FCSTD DOCUMENT  (FreeCAD 0.18R16117 (Git))
Label: impianto_1
License: All rights reserved
LicenseURL: http://en.wikipedia.org/wiki/All_rights_reserved
objects: Sketcher::SketchObject×1, PartDesign::Body×1, Drawing::FeatureViewPart×1, Drawing::FeaturePage×1
note: 2 computed .brp shape members not serialized (recipe doc carries the construction recipe); baked Part::Feature solids carry a one-line shape summary decoded from their .brp

FEATURE [Sketcher::SketchObject] Sketch
  MapMode = 5
  Support = -> [XY_Plane]
  sketch-geometry (29):
    g0: LineSegment StartX=10 StartY=0 StartZ=0 EndX=10 EndY=17 EndZ=0
    g1: LineSegment StartX=0 StartY=17 StartZ=0 EndX=0 EndY=0 EndZ=0
    g2: LineSegment StartX=83.6635 StartY=45.5185 StartZ=0 EndX=83.6635 EndY=27.5185 EndZ=0
    g3: LineSegment StartX=63.9673 StartY=42.0455 StartZ=0 EndX=83.6635 EndY=45.5185 EndZ=0
    g4: LineSegment StartX=83.6635 StartY=27.5185 StartZ=0 EndX=63.9673 EndY=30.9915 EndZ=0
    g5: Circle CenterX=83.6635 CenterY=13.7593 CenterZ=0 NormalX=0 NormalY=0 NormalZ=1 AngleXU=0 Radius=3
    g6: LineSegment [constr] StartX=83.6635 StartY=16.7593 StartZ=0 EndX=83.6635 EndY=10.7593 EndZ=0
    g7: LineSegment StartX=0 StartY=17 StartZ=0 EndX=5 EndY=17 EndZ=0
    g8: LineSegment StartX=10 StartY=17 StartZ=0 EndX=5 EndY=17 EndZ=0
    g9: LineSegment StartX=0 StartY=0 StartZ=0 EndX=5 EndY=0 EndZ=0
    g10: LineSegment StartX=5 StartY=0 StartZ=0 EndX=10 EndY=0 EndZ=0
    g11: LineSegment StartX=83.6635 StartY=10.7593 StartZ=0 EndX=83.6635 EndY=0 EndZ=0
    g12: LineSegment StartX=83.6635 StartY=0 StartZ=0 EndX=44.3317 EndY=0 EndZ=0
    g13: LineSegment StartX=83.6635 StartY=16.7593 StartZ=0 EndX=83.6635 EndY=27.5185 EndZ=0
    g14: LineSegment StartX=63.9673 StartY=42.0455 StartZ=0 EndX=63.9673 EndY=36.5185 EndZ=0
    g15: LineSegment StartX=63.9673 StartY=36.5185 StartZ=0 EndX=63.9673 EndY=30.9915 EndZ=0
    g16: LineSegment StartX=5 StartY=53.742 StartZ=0 EndX=5 EndY=17 EndZ=0
    g17: LineSegment StartX=36.3317 StartY=-8.89633 StartZ=0 EndX=44.3317 EndY=-8.89633 EndZ=0
    g18: LineSegment StartX=44.3317 StartY=-8.89633 StartZ=0 EndX=52.3317 EndY=-8.89633 EndZ=0
    g19: LineSegment StartX=52.3317 StartY=-14.8963 StartZ=0 EndX=44.3317 EndY=-14.8963 EndZ=0
    g20: LineSegment StartX=44.3317 StartY=-14.8963 StartZ=0 EndX=36.3317 EndY=-14.8963 EndZ=0
    g21: ArcOfCircle CenterX=36.3317 CenterY=-11.8963 CenterZ=0 NormalX=0 NormalY=0 NormalZ=1 AngleXU=0 Radius=3 StartAngle=1.5708 EndAngle=4.71239
    g22: ArcOfCircle CenterX=52.3317 CenterY=-11.8963 CenterZ=0 NormalX=0 NormalY=0 NormalZ=1 AngleXU=0 Radius=3 StartAngle=4.71239 EndAngle=7.85398
    g23: LineSegment StartX=44.3317 StartY=0 StartZ=0 EndX=44.3317 EndY=-8.89633 EndZ=0
    g24: LineSegment StartX=44.3317 StartY=-14.8963 StartZ=0 EndX=44.3317 EndY=-23.7927 EndZ=0
    g25: LineSegment StartX=44.3317 StartY=-23.7927 StartZ=0 EndX=5 EndY=-23.7927 EndZ=0
    g26: LineSegment StartX=5 StartY=-23.7927 StartZ=0 EndX=5 EndY=0 EndZ=0
    g27: LineSegment StartX=63.9673 StartY=42.0455 StartZ=0 EndX=63.9673 EndY=53.742 EndZ=0
    g28: LineSegment StartX=63.9673 StartY=53.742 StartZ=0 EndX=5 EndY=53.742 EndZ=0
  constraints (81):
    c: Vertical(g0)
    c: Vertical(g1)
    c: Vertical(g2)
    c: Coincident(g3,g2)
    c: Coincident(g4,g2)
    c: Equal(g3,g4)
    c: PointOnObject(g6,g5)
    c: PointOnObject(g6,g5)
    c: Vertical(g6)
    c: PointOnObject(g5,g6)
    c: Radius(g5) = 3
    c: Distance(g4) = 20
    c: Coincident(g7,g1)
    c: Horizontal(g7)
    c: Coincident(g8,g0)
    c: Coincident(g8,g7)
    c: Horizontal(g8)
    c: Coincident(g9,g1)
    c: Horizontal(g9)
    c: Coincident(g10,g9)
    c: Coincident(g10,g0)
    c: Horizontal(g10)
    c: Equal(g10,g9)
    c: Equal(g8,g7)
    c: Coincident(g1,g-1)
    c: Coincident(g11,g6)
    c: Vertical(g11)
    c: Coincident(g12,g11)
    c: Horizontal(g12)
    c: Coincident(g13,g6)
    c: Coincident(g13,g2)
    c: Vertical(g13)
    c: Coincident(g14,g3)
    c: Vertical(g14)
    c: Coincident(g15,g14)
    c: Coincident(g15,g4)
    c: Vertical(g15)
    c: Equal(g15,g14)
    c: Coincident(g16,g7)
    c: Vertical(g16)
    c: Coincident(g18,g17)
    c: Coincident(g20,g19)
    c: Equal(g19,g20)
    c: Equal(g18,g17)
    c: Horizontal(g18)
    c: Horizontal(g17)
    c: Horizontal(g20)
    c: Horizontal(g19)
    c: Coincident(g21,g17)
    c: Coincident(g21,g20)
    c: Coincident(g22,g18)
    c: Coincident(g22,g19)
    c: Vertical(g17,g19)
    c: Equal(g17,g20)
    c: Equal(g22,g21)
    c: Vertical(g22,g18)
    c: Distance(g17) = 8
    c: Radius(g21) = 3
    c: Coincident(g23,g12)
    c: Coincident(g23,g17)
    c: Vertical(g23)
    c: Coincident(g24,g19)
    c: Vertical(g24)
    c: Coincident(g25,g24)
    c: Horizontal(g25)
    c: Coincident(g26,g25)
    c: Coincident(g26,g9)
    c: Vertical(g26)
    c: Angle(g4,g15) = 1.74533
    c: Equal(g13,g11)
    c: Equal(g12,g25)
    c: Equal(g23,g24)
    c: Distance(g0) = 17
    c: Distance(g7) = 5
    c: PointOnObject(g12,g-1)
    c: Distance(g2) = 18
    c: Coincident(g27,g3)
    c: Vertical(g27)
    c: Coincident(g28,g27)
    c: Horizontal(g28)
    c: Coincident(g28,g16)
FEATURE [PartDesign::Body] Body
  Group = -> [Sketch]
  Origin = -> Origin
FEATURE [Drawing::FeatureViewPart] View
  Direction = (0,0,1)
  HiddenWidth = 0.15
  LineWidth = 0.3
  Rotation = 0
  ShowHiddenLines = false
  ShowSmoothLines = false
  Source = -> Sketch
  Tolerance = 0.05
  ViewResult = <g id="View"\n   transform="rotate(0,40,100) translate(40,100) scale(1,1)"\n  >\n<g   fill="none"\n   stroke="rgb(0, 0, 0)"\n   stroke-linecap="butt"\n   stroke-linejoin="miter"\n   stroke-width="0.300000"\n   transform="scale(1,-1)"\n  >\n<path id= "1" d=" M -6.00422e-33 17 L -6.00422e-33 0 " />\n<path id= "2" d=" M -6.00422e-33 0 L 5 0 " />\n<path id= "3" d=" M 5 -23.7927 L 5 0 " />\n<path id= "4" d=" M 44.3317 -23.7927 L 5 -23.7927 " />\n<path id= "5" d=" M 44.3317 -14.8963 L 44.3317 -23.7927 " />\n<path id= "6" d=" M 44.3317 -8.89633 L 52.3317 -8.89633 " />\n<path d="M52.3317 -14.8963 A3 3 0 0 1 52.3317 -8.89633" /><path id= "8" d=" M 52.3317 -14.8963 L 44.3317 -14.8963 " />\n<path id= "9" d=" M 44.3317 -14.8963 L 36.3317 -14.8963 " />\n<path d="M36.3317 -8.89633 A3 3 0 0 1 36.3317 -14.8963" /><path id= "11" d=" M 36.3317 -8.89633 L 44.3317 -8.89633 " />\n<path id= "12" d=" M 44.3317 3.98103e-28 L 44.3317 -8.89633 " />\n<path id= "13" d=" M 83.6635 3.98103e-28 L 44.3317 3.98103e-28 " />\n<path id= "14" d=" M 83.6635 10.7593 L 83.6635 0 " />\n<path id= "15" d=" M 83.6635 16.7593 L 83.6635 27.5185 " />\n<path id= "16" d=" M 83.6635 45.5185 L 83.6635 27.5185 " />\n<path id= "17" d=" M 63.9673 42.0455 L 83.6635 45.5185 " />\n<path id= "18" d=" M 63.9673 42.0455 L 63.9673 36.5185 " />\n<path id= "19" d=" M 83.6635 27.5185 L 63.9673 30.9915 " />\n<path id= "20" d=" M 63.9673 36.5185 L 63.9673 30.9915 " />\n<path id= "21" d=" M 63.9673 42.0455 L 63.9673 53.742 " />\n<path id= "22" d=" M 63.9673 53.742 L 5 53.742 " />\n<path id= "23" d=" M 5 53.742 L 5 17 " />\n<path id= "24" d=" M 5 0 L 10 0 " />\n<path id= "25" d=" M 10 0 L 10 17 " />\n<path id= "26" d=" M 10 17 L 5 17 " />\n<path id= "27" d=" M -6.00422e-33 17 L 5 17 " />\n<circle cx ="83.6635" cy ="13.7593" r ="3" /></g>\n</g>
  Visible = true
  X = 40
  Y = 100
FEATURE [Drawing::FeaturePage] Page
  Group = -> [View]
  Template = <path>
note: 1 file-system path scrubbed to <path> (originals preserved in the JSON sidecar)
